# Revit family: HVAC_HangingSystems_Walraven_BIS_RapidStrut_Rail_Connector − U-shaped_G2_(BUP1000)
name_source: partatom
category: Mechanical Equipment
revit_build: Autodesk Revit MEP 2016 (Build: 20150220_1215(x64)
units: mm (PartAtom-declared; Revit-internal decimal feet)

## family parameters
Always vertical = No
Cut with Voids When Loaded = No
OmniClass Number = 23.60.30.11.17
OmniClass Title = Pipework/Ductwork Mechanical Fasteners/Supports
Part Type = Normal
Room Calculation Point = No
Round Connector Dimension = Use Diameter
Shared = No
Work Plane-Based = Yes

## types (1)
- std
    Assembly Code = 50
    BIMobject category = Hanging Systems
    BIMobject category code = hvac-hanging-systems
    BIMobject main category = HVAC
    BIMobject main category code = hvac
    Brand url = https://www.walraven.com
    Date of publishing = 7/20/2018
    Default Elevation = 1219 mm
    Description = U-shaped rail connector
    Design country = Netherlands
    Edition number = 0
    IFC Classification = Mechanical Fastener
    IfcDescription = U-shaped rail connector
    IfcExportAs = IfcMechanicalFastenerType
    IfcExportType = USERDEFINED
    Manufacturer = Walraven
    Manufacturer country = Czech Republic
    Manufacturer name = Walraven
    Material main = Steel
    Model = BIS RapidStrut Rail Connector − U-shaped G2 (BUP1000)
    NLRS_C_code_SfB_tabel1 = 50
    NLRS_C_niveau_ontwikkeling = LOD400
    Nominal height = 21 mm  [stored 0.0688976 ft]
    Nominal width = 42 mm
    OmniClass Code = 23-27 43 13
    OmniClass Description = Mechanical Pipe Supports
    Product Guid = 4ca4e894-9860-4a08-a501-27765336d389
    Product SKU = bis-rapidstrut-rail-connector-u-shaped-g2-bup1000
    Product data url = https://bimobject.com
    Product family = Rail Systems
    Product group = Rail Connectors
    Product url = https://www.walraven.com
    QR code = http://bimobject.com
    RSen_C_code_ETIM = EC000483
    RSen_C_code_ETIM_url = https://prod.etim-international.com
    RSen_C_content_modification_date = 04-06-2018
    RSen_C_content_releasedate = 04-06-2018
    RSen_C_intended_use = hanging systems
    RSen_C_material = steel
    RSen_C_material_01 = Polyoxymethylene (POM)
    RSen_C_material_colour = grey+green
    RSen_C_material_finish = BIS UltraProtect® 1000
    RSen_S_max_torque = 15
    Technical description = https://library.walraven.com
    URL = https://www.walraven.com
    Weight Net (Kg) = 0.745
    region_index = 1

note: [stored X ft] marks values corroborated as IEEE doubles in the binary element streams (Revit-internal decimal feet)

## geometry (parser evidence)
native form markers: Blend x4, Sweep x15
no freeform markers — native parametric forms only
